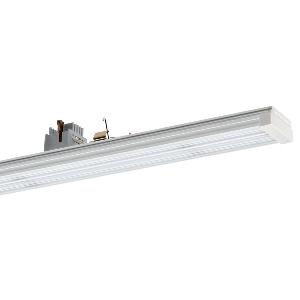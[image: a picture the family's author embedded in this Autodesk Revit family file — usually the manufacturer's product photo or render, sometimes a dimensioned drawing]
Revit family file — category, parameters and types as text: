
# Revit family: conveo_-_cvg_15000_840_w-p_ea_5_226848119-00804947_baa0
name_source: partatom
category: Lighting Fixtures
units: mm (PartAtom-declared; Revit-internal decimal feet)

## family parameters
Cut with Voids When Loaded = No
Host = Face
Light Source = No
Part Type = Normal
Room Calculation Point = No
Round Connector Dimension = Use Diameter
Shared = No

## types (1)
- CONVEO - CVG 15000/840/W-P/EA/5 (1 x LED, 14700 lm, 4000K)
    Apparent Load = 100 VA
    Approval mark = CE
    CIE Flux Codes = 54 85 97 100 100
    Color Rendering = 80-89
    Color Temperature = 4000K
    Control Gear = Electronic ballast
    Default Elevation = 1800 mm
    Description = CVG 15000/840/W-P/EA/5|Continuous-row system|light source: LED|work equipment: Electronic ballast|connected load: 220-240 V, 50-60 Hz|Power consumption: approx. 100 W|luminous flux: 14700 lm|luminous efficacy: 147 lm/W|colour temperature: Cold white, ca. 4000 K|color rendering index (CRI): >= 80|chromaticity tolerance:  3 SDCM|System of protection: IP 54|class of protection: I|technology: Switchable|luminaire body|material: Aluminium|surface: Powder coatet|colour: White|lamp cover: Acrylic (PMMA), Satine|weight (net): approx. 2.2 kg|Fastening: Available separately|minimum ambient temperature: -25 ░C|maximum ambient temperature: 37 ░C|glare control: Prism optics (linear)|Approval mark: VDE - ENEC|
    Frequency = 50 Hz
    Height = 70 mm
    Lamp = 1 x LED
    Lamp Light Flux = 14700 lm
    Lamp count = 1
    Length = 1500 mm
    Luminous efficacy = 147 lm/W
    Manufacturer = Waldmann
    ModVariant = No
    Model = 226848119-00804947
    Mounting Place = Ceiling
    Mounting Type = Pendant
    Number of Poles = 1
    OnlyDefault = Yes
    Power Factor = 1
    Product Name = CONVEO - CVG 15000/840/W-P/EA/5
    Product group = Continuous-row system (industry)
    ProductGroupID = 301
    Protection Class = Protection class I
    Protection Degree = IP 54
    RLX_Detail_Level = 1
    RlxData = <blob elided: 132917 chars, md5=5521dc39>
    Socket = socket
    Standby Power = 0 W
    System Light Flux = 14700 lm
    System Power = 100 W
    Type Comments = Product without accessories
    Type Image = 226848119-00804947-2p5.jpg
    URL = http://relux.com
    VarID = ---
    Voltage = 230 V
    Voltage Range = 220-240 V
    Weight = 0.00 kg
    Width = 64 mm

## geometry (parser evidence)
native form markers: Blend x4, Sweep x8
no freeform markers — native parametric forms only
